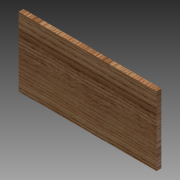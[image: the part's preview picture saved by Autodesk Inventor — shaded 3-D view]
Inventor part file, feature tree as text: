
AUTODESK INVENTOR PART (.ipt)
format: ipt  version: 2012 (Build 160160000, 160)  size: 92,672 bytes
history: native  units: in
note: dims shown in document units (in); Inventor stores cm internally (conversion verified against a paired STEP export)
features: extrude x1, sketch x1
ambient origin geometry x8: Origin, YZ Plane, XZ Plane, XY Plane, X Axis, Y Axis, Z Axis, Center Point
bodies: Solid1 (feature_tree)
feature tree (2):
  extrude  "Extrusion1"  Depth=3.5in
  sketch  "Sketch1"  dims[d0=7.0in d1=3.5in d2=0.25in d3=0.0in]
